# Revit family: TESK_Насос вертикальный_TK300
name_source: partatom
category: Оборудование
units: mm (PartAtom-declared; Revit-internal decimal feet)

## family parameters
Всегда вертикально = Да
Классификация = Насос
На основе рабочей плоскости = Нет
Общий = Нет
При загрузке вырезать с полостями = Нет
Размер круглого соединителя = Использовать диаметр
Тип детали = Вставляется
Точка расчета площади = Нет

## types (7) — shared parameters
ADSK_URL документации изделия = https://teskpump.ru
ADSK_Диаметр условный = 300 мм
ADSK_Единица измерения = шт.
ADSK_Завод-изготовитель = TESK
ADSK_Классификация нагрузок = Прочее
ADSK_Количество = 1
ADSK_Количество фаз = 3
ADSK_Количество фаз числовое = 3
ADSK_Коэффициент мощности = 1
ADSK_Напряжение = 400 В
C = 185 мм
DN = 300 мм
F0 = 460 мм
F1 = 370 мм
F2 = 185 мм
F3 = 287.5 мм
F4 = 340.74 мм
H1 = 290 мм
L1 = 1200 мм
URL = https://teskpump.ru
Изготовитель = TESK
Материал_1 = TESK_Черный_Условный
Материал_2 = TESK_Черный_Ребра_Условный
Плита_Толщина = 35 мм
Энергоэффективность = IE3

## per-type parameters (varying)
| type | ADSK_Код изделия | ADSK_Масса | ADSK_Масса_Текст | ADSK_Наименование | ADSK_Номинальная мощность | ADSK_Полная мощность | B1 | B2 | B3 | B4 | B5 | D | D2 | D3 | H2 | H3 | H4 | Напор максимальный | Плита_Глубина | Плита_Ширина |
| ТК 300-15/4  55kW 3x380V 50Hz IE3 | 55TK30015403380 | 907 | 907 | Вертикальный насос TESK типа IN-LINE, DN300, Hmax=15м (3x380V 50Hz IE3) | 55.00 кВт | 55.00 кВ·А | 490 мм | 365 мм | 345 мм | 250 мм | 440 мм | 550 мм | 335 мм | 400 мм | 649 мм | 1720 мм | 781 мм | 15 | 484 мм | 484 мм |
| ТК 300-20/4  75kW 3x380V 50Hz IE3 | 55TK30020403380 | 1075 | 1075 | Вертикальный насос TESK типа IN-LINE, DN300, Hmax=20м (3x380V 50Hz IE3) | 75.00 кВт | 75.00 кВ·А | 550 мм | 400 мм | 345 мм | 250 мм | 440 мм | 550 мм | 370 мм | 400 мм | 649 мм | 1770 мм | 831 мм | 20 | 484 мм | 484 мм |
| ТК 300-25/4  90kW 3x380V 50Hz IE3 | 55TK30025403380 | 1230 | 1230 | Вертикальный насос TESK типа IN-LINE, DN300, Hmax=25м (3x380V 50Hz IE3) | 90.00 кВт | 90.00 кВ·А | 550 мм | 400 мм | 380 мм | 280 мм | 480 мм | 550 мм | 370 мм | 460 мм | 659 мм | 1850 мм | 901 мм | 25 | 524 мм | 524 мм |
| ТК 300-30/4  110kW 3x380V 50Hz IE3 | 55TK30030403380 | 1570 | 1570 | Вертикальный насос TESK типа IN-LINE, DN300, Hmax=30м (3x380V 50Hz IE3) | 110.00 кВт | 110.00 кВ·А | 625 мм | 550 мм | 380 мм | 280 мм | 480 мм | 660 мм | 520 мм | 460 мм | 699 мм | 2000 мм | 1011 мм | 30 | 524 мм | 524 мм |
| ТК 300-35/4  132kW 3x380V 50Hz IE3 | 55TK30035403380 | 1650 | 1650 | Вертикальный насос TESK типа IN-LINE, DN300, Hmax=35м (3x380V 50Hz IE3) | 132.00 кВт | 132.00 кВ·А | 625 мм | 550 мм | 380 мм | 280 мм | 480 мм | 660 мм | 520 мм | 460 мм | 699 мм | 2150 мм | 1161 мм | 35 | 524 мм | 524 мм |
| ТК 300-44/4  160kW 3x380V 50Hz IE3 | 55TK30044403380 | 1790 | 1790 | Вертикальный насос TESK типа IN-LINE, DN300, Hmax=44м (3x380V 50Hz IE3) | 160.00 кВт | 160.00 кВ·А | 625 мм | 550 мм | 380 мм | 280 мм | 480 мм | 660 мм | 520 мм | 460 мм | 702 мм | 2150 мм | 1158 мм | 44 | 524 мм | 524 мм |
| ТК 300-55/4  200kW 3x380V 50Hz IE3 | 55TK30055403380 | 1905 | 1905 | Вертикальный насос TESK типа IN-LINE, DN300, Hmax=55м (3x380V 50Hz IE3) | 200.00 кВт | 200.00 кВ·А | 625 мм | 550 мм | 380 мм | 280 мм | 480 мм | 660 мм | 520 мм | 460 мм | 702 мм | 2150 мм | 1158 мм | 55 | 524 мм | 524 мм |

note: column(s) folded — value = type name in every type: ADSK_Марка
